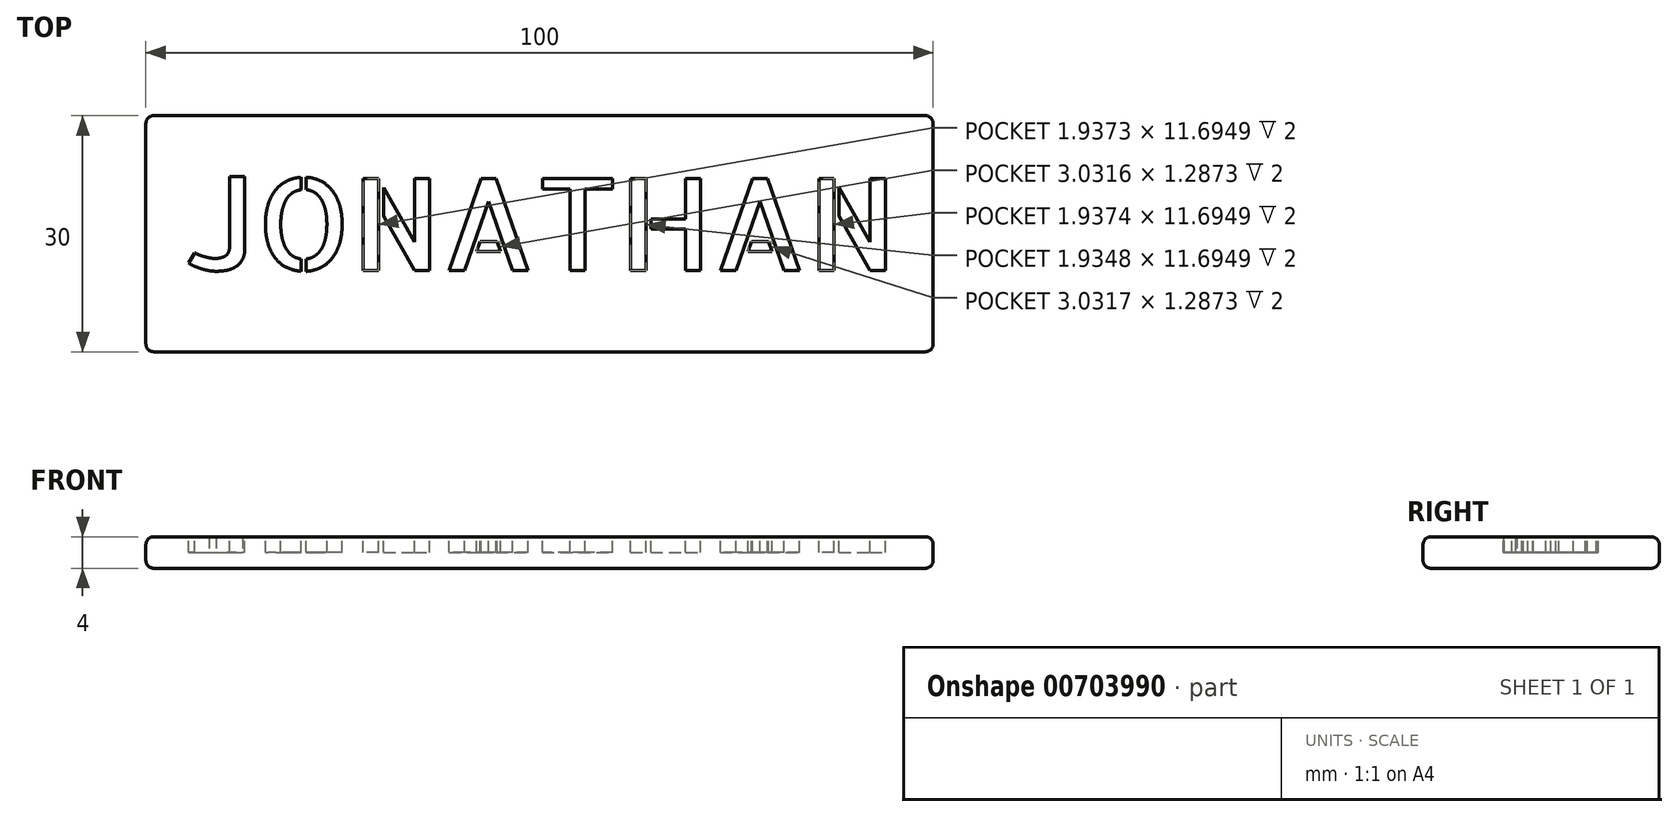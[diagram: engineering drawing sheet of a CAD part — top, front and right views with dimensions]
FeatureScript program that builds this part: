
annotation { "Feature Type Name" : "Feature", "Feature Type Description" : "" }
export const myFeature = defineFeature(function(context is Context, id is Id, definition is map)
    precondition{}
    {
        {
            var Q0;
            Q0=qCreatedBy(makeId("Top.planeOp"),FACE);
            var sketch = newSketch(context, id + "F0", { "sketchPlane" : qUnion([Q0])});
            skLineSegment(sketch, "E0.bottom", {"start": v(50, 15) * mm, "end": v(-50, 15) * mm});
            skLineSegment(sketch, "E0.top", {"start": v(50, -15) * mm, "end": v(-50, -15) * mm});
            skLineSegment(sketch, "E0.left", {"start": v(50, 15) * mm, "end": v(50, -15) * mm});
            skLineSegment(sketch, "E0.right", {"start": v(-50, 15) * mm, "end": v(-50, -15) * mm});
            skPoint(sketch, "E0.middle", {"position": v(0, 0) * mm});
            skSolve(sketch);
        }
        {
            var Q0;
            Q0=makeQuery(id+"F0.imprint","IMPRINT",FACE,{"disambiguationData":[TD([[makeQuery(id+"F0.imprint","IMPRINT",EDGE,{"derivedFrom":sQuery(id+"F0.wireOp",EDGE,"E0.bottom")}),1.0]])]});
            extrude(context, id + "F1", {"entities" : qUnion([Q0]), "oppositeDirection" : true, "depth" : 4 * mm, "offsetDistance" : 25 * mm});
        }
        {
            var Q0;
            Q0=qCreatedBy(makeId("Top.planeOp"),FACE);
            var sketch = newSketch(context, id + "F2", { "sketchPlane" : qUnion([Q0])});
            skText(sketch, "E1", { "text": "JONATHAN\n", "fontName": "AllertaStencil-Regular.ttf"});
            const initialGuessF2  = {"E1": [-0.045, -0.0047, 1, 0, 0.0117]};
            skSetInitialGuess(sketch, initialGuessF2);
            skSolve(sketch);
        }
        {
            var Q0;
            Q0=qSketchRegion(id+"F2",true);
            extrude(context, id + "F3", {"entities" : qUnion([Q0]), "operationType" : NewBodyOperationType.REMOVE, "oppositeDirection" : true, "depth" : 2 * mm, "offsetDistance" : 25 * mm});
        }
        {
            var Q0;
            Q0=makeQuery(id+"F1.opExtrude","CAP_EDGE",EDGE,{"disambiguationData":[OSD([sQuery(id+"F0.wireOp",EDGE,"E0.bottom")])],"isStart":true});
            var Q1;
            Q1=makeQuery(id+"F1.opExtrude","CAP_EDGE",EDGE,{"disambiguationData":[OSD([sQuery(id+"F0.wireOp",EDGE,"E0.bottom")])],"isStart":false});
            var Q2;
            Q2=makeQuery(id+"F1.opExtrude","CAP_EDGE",EDGE,{"disambiguationData":[OSD([sQuery(id+"F0.wireOp",EDGE,"E0.right")])],"isStart":true});
            var Q3;
            Q3=makeQuery(id+"F1.opExtrude","CAP_EDGE",EDGE,{"disambiguationData":[OSD([sQuery(id+"F0.wireOp",EDGE,"E0.right")])],"isStart":false});
            var Q4;
            Q4=makeQuery(id+"F1.opExtrude","SWEPT_EDGE",EDGE,{"disambiguationData":[OSD([sQuery(id+"F0.wireOp",EDGE,"E0.bottom"),sQuery(id+"F0.wireOp",EDGE,"E0.right")])]});
            var Q5;
            Q5=makeQuery(id+"F1.opExtrude","SWEPT_EDGE",EDGE,{"disambiguationData":[OSD([sQuery(id+"F0.wireOp",EDGE,"E0.bottom"),sQuery(id+"F0.wireOp",EDGE,"E0.left")])]});
            var Q6;
            Q6=makeQuery(id+"F1.opExtrude","CAP_EDGE",EDGE,{"disambiguationData":[OSD([sQuery(id+"F0.wireOp",EDGE,"E0.left")])],"isStart":false});
            var Q7;
            Q7=makeQuery(id+"F1.opExtrude","CAP_EDGE",EDGE,{"disambiguationData":[OSD([sQuery(id+"F0.wireOp",EDGE,"E0.left")])],"isStart":true});
            var Q8;
            Q8=makeQuery(id+"F1.opExtrude","SWEPT_EDGE",EDGE,{"disambiguationData":[OSD([sQuery(id+"F0.wireOp",EDGE,"E0.top"),sQuery(id+"F0.wireOp",EDGE,"E0.left")])]});
            var Q9;
            Q9=makeQuery(id+"F1.opExtrude","CAP_EDGE",EDGE,{"disambiguationData":[OSD([sQuery(id+"F0.wireOp",EDGE,"E0.top")])],"isStart":false});
            var Q10;
            Q10=makeQuery(id+"F1.opExtrude","CAP_EDGE",EDGE,{"disambiguationData":[OSD([sQuery(id+"F0.wireOp",EDGE,"E0.top")])],"isStart":true});
            var Q11;
            Q11=makeQuery(id+"F1.opExtrude","SWEPT_EDGE",EDGE,{"disambiguationData":[OSD([sQuery(id+"F0.wireOp",EDGE,"E0.top"),sQuery(id+"F0.wireOp",EDGE,"E0.right")])]});
            fillet(context, id + "F4", {"entities" : qUnion([Q0, Q1, Q2, Q3, Q4, Q5, Q6, Q7, Q8, Q9, Q10, Q11]), "radius" : 1 * mm, "tangentPropagation" : true, "allowEdgeOverflow" : false});
        }
    });
